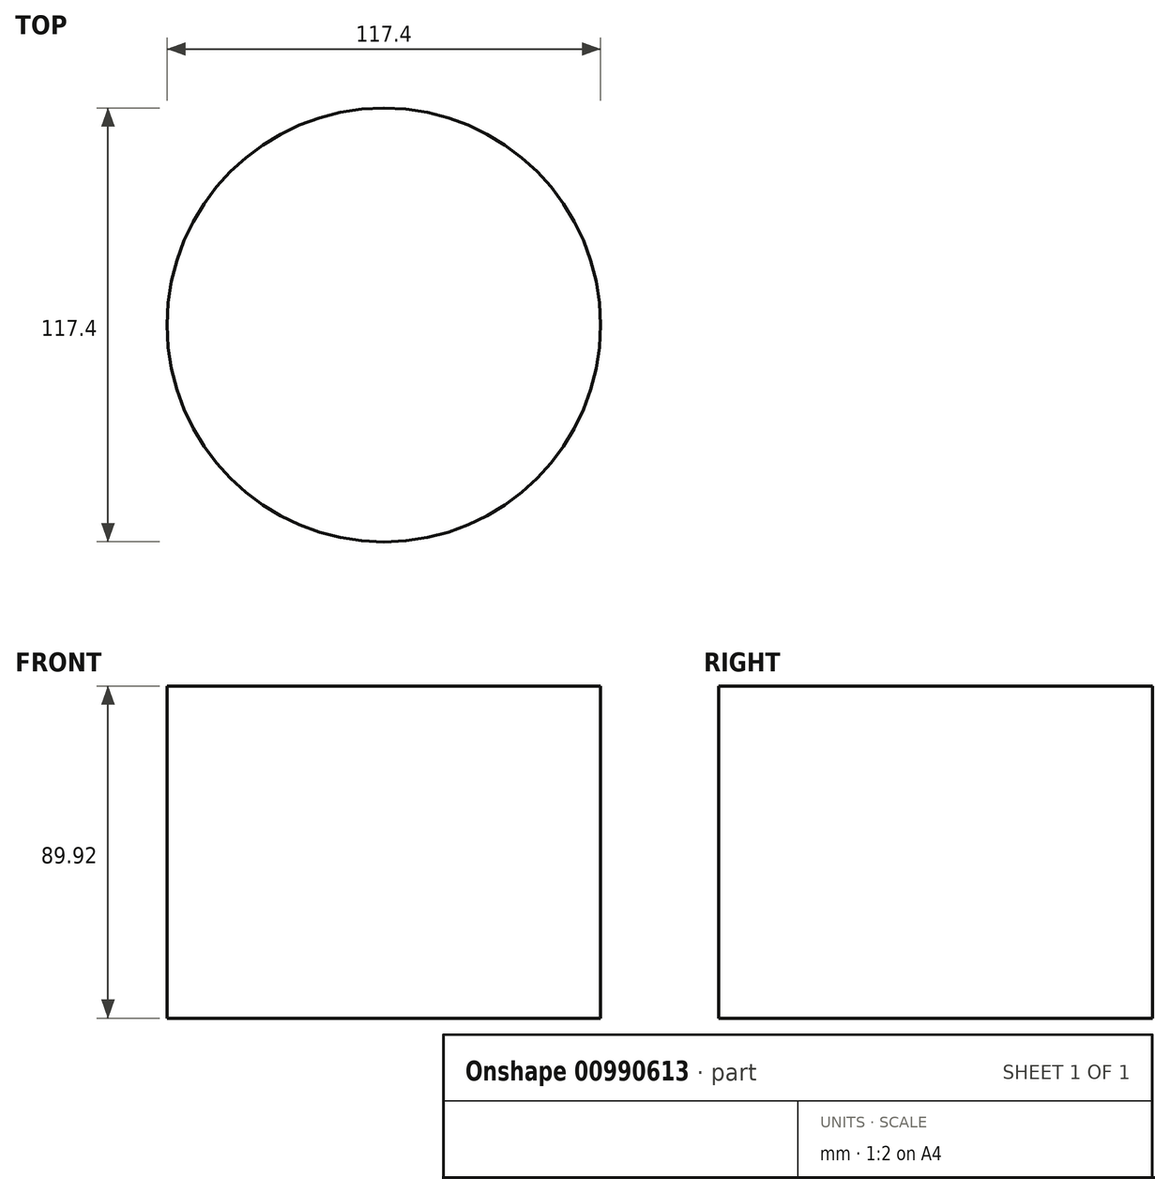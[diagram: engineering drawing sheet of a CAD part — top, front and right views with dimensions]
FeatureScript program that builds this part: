
annotation { "Feature Type Name" : "Feature", "Feature Type Description" : "" }
export const myFeature = defineFeature(function(context is Context, id is Id, definition is map)
    precondition{}
    {
        {
            var Q0;
            Q0=qCreatedBy(makeId("Top.planeOp"),FACE);
            var sketch = newSketch(context, id + "F0", { "sketchPlane" : qUnion([Q0])});
            skCircle(sketch, "E0", {"center": v(0, 0) * mm, "radius": 58.7 * mm});
            skSolve(sketch);
        }
        {
            var Q0;
            Q0=makeQuery(id+"F0.imprint","IMPRINT",FACE,{"disambiguationData":[TD([[makeQuery(id+"F0.imprint","IMPRINT",EDGE,{"derivedFrom":sQuery(id+"F0.wireOp",EDGE,"E0")}),1.0]])]});
            extrude(context, id + "F1", {"entities" : qUnion([Q0]), "oppositeDirection" : true, "depth" : 89.92 * mm, "offsetDistance" : 25.4 * mm});
        }
    });
